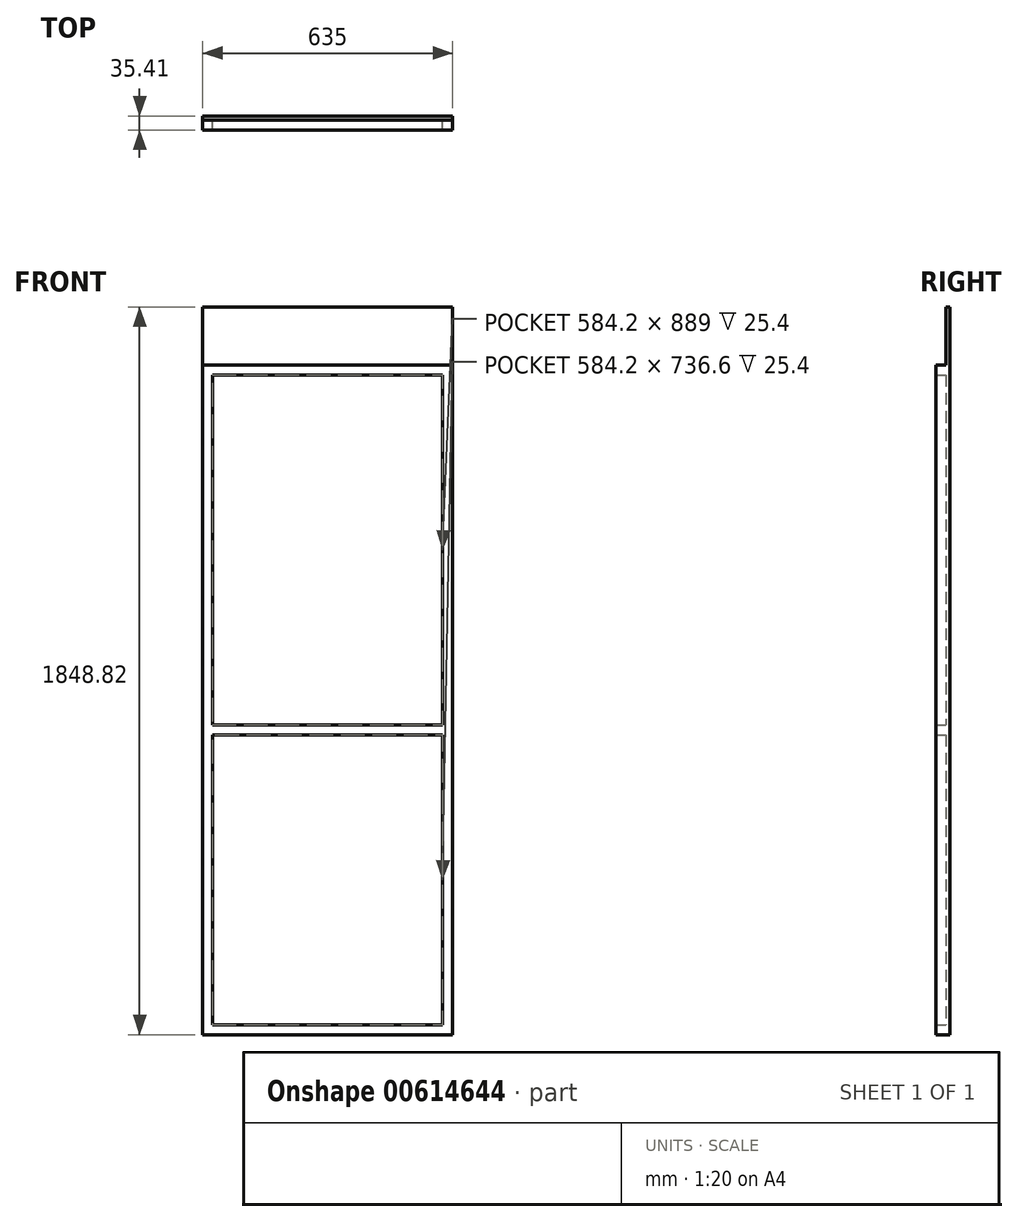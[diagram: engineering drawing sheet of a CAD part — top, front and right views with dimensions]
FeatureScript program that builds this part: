
annotation { "Feature Type Name" : "Feature", "Feature Type Description" : "" }
export const myFeature = defineFeature(function(context is Context, id is Id, definition is map)
    precondition{}
    {
        {
            var Q0;
            Q0=qCreatedBy(makeId("Front.planeOp"),FACE);
            var sketch = newSketch(context, id + "F0", { "sketchPlane" : qUnion([Q0])});
            skLineSegment(sketch, "E0.bottom", {"start": v(-304.82, 1069.9) * mm, "end": v(330.18, 1069.9) * mm});
            skLineSegment(sketch, "E0.top", {"start": v(-304.82, -631.9) * mm, "end": v(330.18, -631.9) * mm});
            skLineSegment(sketch, "E0.left", {"start": v(-304.82, 1069.9) * mm, "end": v(-304.82, -631.9) * mm});
            skLineSegment(sketch, "E0.right", {"start": v(330.18, 1069.9) * mm, "end": v(330.18, -631.9) * mm});
            skSolve(sketch);
        }
        {
            var Q0;
            Q0 = qSketchRegion(id + "F0", true);
            extrude(context, id + "F1", {"entities" : qUnion([Q0]), "depth" : 10 * mm, "offsetDistance" : 25.4 * mm});
        }
        {
            var Q0;
            Q0=makeQuery(id+"F1.opExtrude","CAP_FACE",FACE,{"disambiguationData":[OSD([sQuery(id+"F0.wireOp",EDGE,"E0.bottom"),sQuery(id+"F0.wireOp",EDGE,"E0.top"),sQuery(id+"F0.wireOp",EDGE,"E0.left"),sQuery(id+"F0.wireOp",EDGE,"E0.right")])],"isStart":false});
            var sketch = newSketch(context, id + "F2", { "sketchPlane" : qUnion([Q0])});
            skLineSegment(sketch, "E1.bottom", {"start": v(-304.82, 1069.9) * mm, "end": v(330.18, 1069.9) * mm});
            skLineSegment(sketch, "E1.top", {"start": v(-304.82, -631.9) * mm, "end": v(330.18, -631.9) * mm});
            skLineSegment(sketch, "E1.left", {"start": v(-304.82, 1069.9) * mm, "end": v(-304.82, -631.9) * mm});
            skLineSegment(sketch, "E1.right", {"start": v(330.18, 1069.9) * mm, "end": v(330.18, -631.9) * mm});
            skLineSegment(sketch, "E2.bottom", {"start": v(-279.42, 1044.5) * mm, "end": v(304.78, 1044.5) * mm});
            skLineSegment(sketch, "E2.top", {"start": v(-279.42, -606.5) * mm, "end": v(304.78, -606.5) * mm});
            skLineSegment(sketch, "E2.left", {"start": v(-279.42, 1044.5) * mm, "end": v(-279.42, 155.5) * mm});
            skLineSegment(sketch, "E2.right", {"start": v(304.78, 1044.5) * mm, "end": v(304.78, 155.5) * mm});
            skLineSegment(sketch, "E3", {"start": v(304.78, 155.5) * mm, "end": v(-279.42, 155.5) * mm});
            skLineSegment(sketch, "E4", {"start": v(-279.42, 130.1) * mm, "end": v(304.78, 130.1) * mm});
            skLineSegment(sketch, "E5.trimOffspring", {"start": v(304.78, 130.1) * mm, "end": v(304.78, -606.5) * mm});
            skLineSegment(sketch, "E6.trimOffspring", {"start": v(-279.42, 130.1) * mm, "end": v(-279.42, -606.5) * mm});
            skSolve(sketch);
        }
        {
            var Q0;
            Q0=makeQuery(id+"F2.imprint","IMPRINT",FACE,{"disambiguationData":[TD([[makeQuery(id+"F2.imprint","IMPRINT",EDGE,{"derivedFrom":sQuery(id+"F2.wireOp",EDGE,"E1.bottom")}),-1.0]])]});
            extrude(context, id + "F3", {"entities" : qUnion([Q0]), "depth" : 25.4 * mm, "offsetDistance" : 25.4 * mm});
        }
        {
            var Q0;
            Q0=makeQuery(id+"F1.opExtrude","SWEPT_FACE",FACE,{"disambiguationData":[OSD([sQuery(id+"F0.wireOp",EDGE,"E0.bottom")])]});
            var sketch = newSketch(context, id + "F4", { "sketchPlane" : qUnion([Q0])});
            skLineSegment(sketch, "E7.bottom", {"start": v(-304.82, 0) * mm, "end": v(330.18, 0) * mm});
            skLineSegment(sketch, "E7.top", {"start": v(-304.82, -10) * mm, "end": v(330.18, -10) * mm});
            skLineSegment(sketch, "E7.left", {"start": v(-304.82, 0) * mm, "end": v(-304.82, -10) * mm});
            skLineSegment(sketch, "E7.right", {"start": v(330.18, 0) * mm, "end": v(330.18, -10) * mm});
            skSolve(sketch);
        }
        {
            var Q0;
            Q0=makeQuery(id+"F4.imprint","IMPRINT",FACE,{"disambiguationData":[TD([[makeQuery(id+"F4.imprint","IMPRINT",EDGE,{"derivedFrom":sQuery(id+"F4.wireOp",EDGE,"E7.bottom")}),-1.0]])]});
            extrude(context, id + "F5", {"entities" : qUnion([Q0]), "operationType" : NewBodyOperationType.ADD, "depth" : 147.02 * mm, "offsetDistance" : 25.4 * mm});
        }
    });
